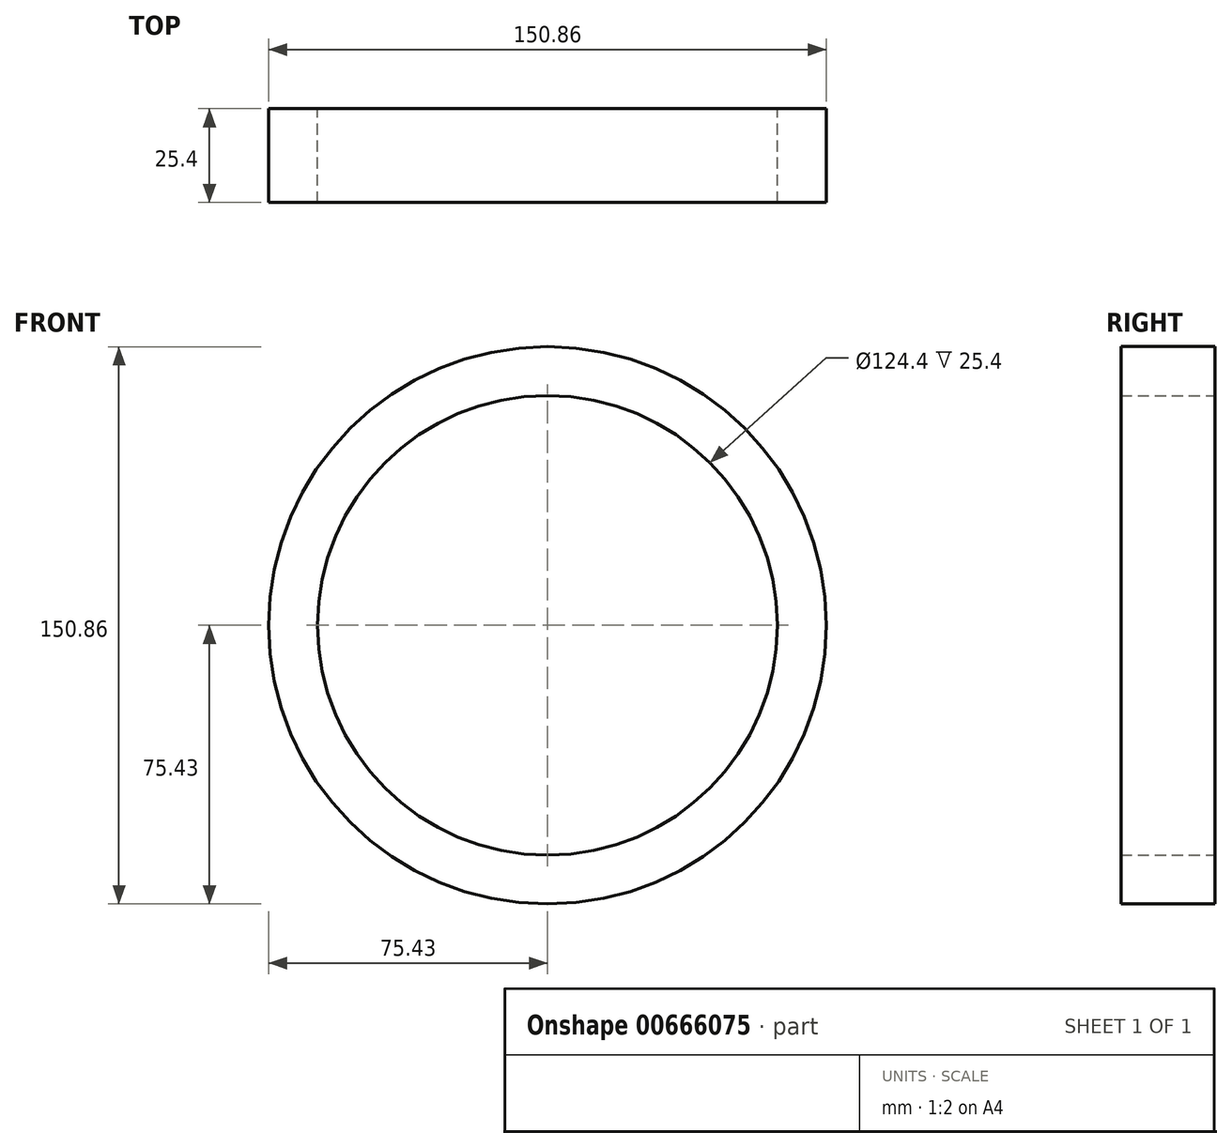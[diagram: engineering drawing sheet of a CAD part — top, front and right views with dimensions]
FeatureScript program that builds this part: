
annotation { "Feature Type Name" : "Feature", "Feature Type Description" : "" }
export const myFeature = defineFeature(function(context is Context, id is Id, definition is map)
    precondition{}
    {
        {
            var Q0;
            Q0=qCreatedBy(makeId("Front.planeOp"),FACE);
            var sketch = newSketch(context, id + "F0", { "sketchPlane" : qUnion([Q0])});
            skCircle(sketch, "E0", {"center": v(0, 0) * mm, "radius": 62.2 * mm});
            skCircle(sketch, "E1", {"center": v(0, 0) * mm, "radius": 75.43 * mm});
            skSolve(sketch);
        }
        {
            var Q0;
            Q0 = qSketchRegion(id + "F0", true);
            extrude(context, id + "F1", {"entities" : qUnion([Q0]), "depth" : 25.4 * mm, "offsetDistance" : 25.4 * mm});
        }
    });
